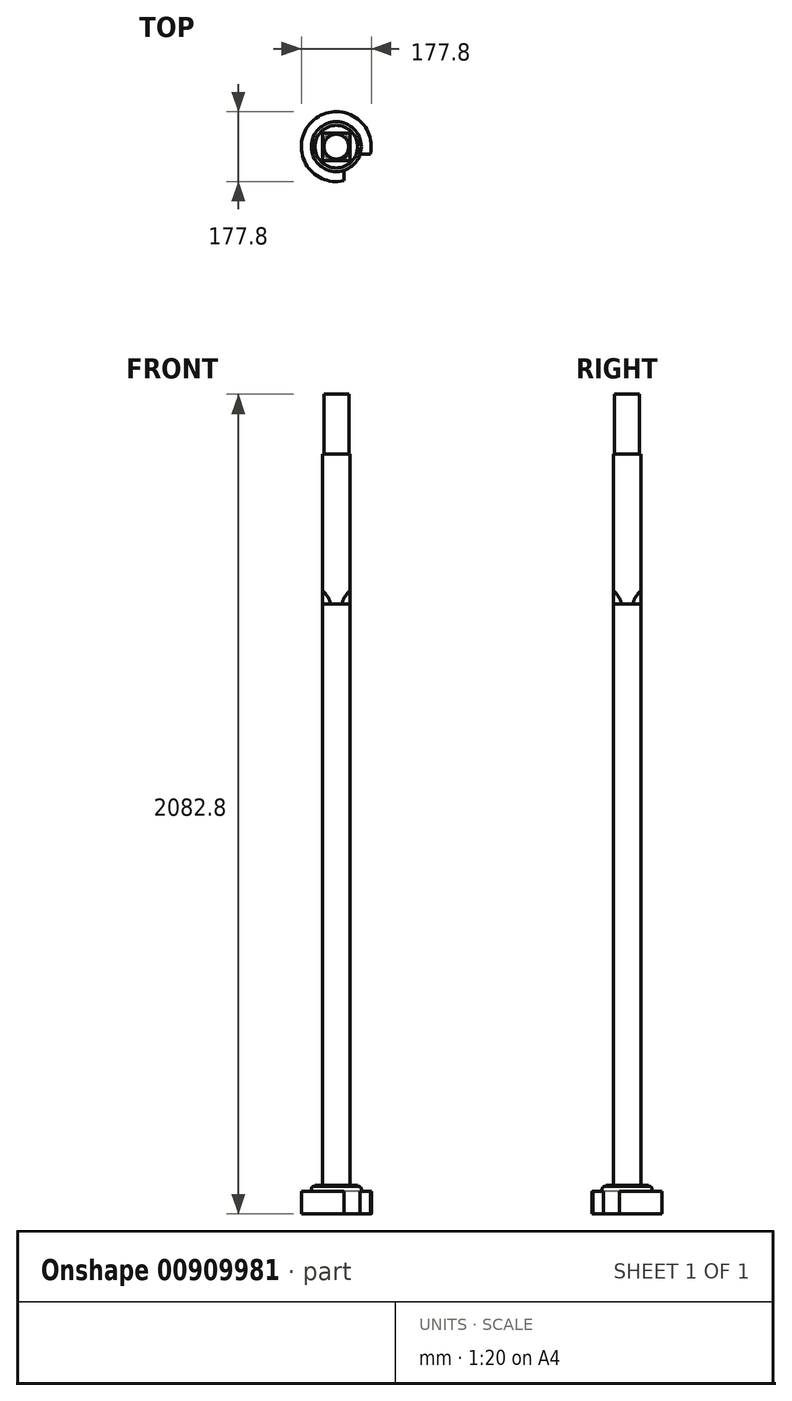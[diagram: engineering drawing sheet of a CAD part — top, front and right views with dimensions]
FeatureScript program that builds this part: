
annotation { "Feature Type Name" : "Feature", "Feature Type Description" : "" }
export const myFeature = defineFeature(function(context is Context, id is Id, definition is map)
    precondition{}
    {
        {
            var Q0;
            Q0=qCreatedBy(makeId("Front.planeOp"),FACE);
            var sketch = newSketch(context, id + "F0", { "sketchPlane" : qUnion([Q0])});
            skLineSegment(sketch, "E0.bottom", {"start": v(0, 0) * mm, "end": v(88.9, 0) * mm});
            skLineSegment(sketch, "E0.top", {"start": v(63.5, 57.15) * mm, "end": v(88.9, 57.15) * mm});
            skLineSegment(sketch, "E0.right", {"start": v(88.9, 0) * mm, "end": v(88.9, 57.15) * mm});
            skLineSegment(sketch, "E1.left", {"start": v(0, 0) * mm, "end": v(0, 1549.4) * mm});
            skLineSegment(sketch, "E1.right", {"start": v(34.92, 0) * mm, "end": v(34.92, 1549.4) * mm});
            skLineSegment(sketch, "E2.bottom", {"start": v(34.92, 1549.4) * mm, "end": v(-34.93, 1549.4) * mm});
            skLineSegment(sketch, "E2.top", {"start": v(34.92, 1930.4) * mm, "end": v(-34.93, 1930.4) * mm});
            skLineSegment(sketch, "E2.left", {"start": v(34.92, 1549.4) * mm, "end": v(34.92, 1930.4) * mm});
            skLineSegment(sketch, "E2.right", {"start": v(-34.93, 1549.4) * mm, "end": v(-34.93, 1930.4) * mm});
            skLineSegment(sketch, "E3", {"start": v(0, 0) * mm, "end": v(0, -15.12) * mm, "construction": true});
            skLineSegment(sketch, "E4.top", {"start": v(0, 2082.8) * mm, "end": v(31.75, 2082.8) * mm});
            skLineSegment(sketch, "E4.left", {"start": v(0, 1930.4) * mm, "end": v(0, 2082.8) * mm});
            skLineSegment(sketch, "E4.right", {"start": v(31.75, 1930.4) * mm, "end": v(31.75, 2082.8) * mm});
            skCircle(sketch, "E5", {"center": v(95.25, 1549.4) * mm, "radius": 57.15 * mm});
            skLineSegment(sketch, "E6", {"start": v(63.5, 57.15) * mm, "end": v(63.5, 63.5) * mm});
            skLineSegment(sketch, "E7", {"start": v(57.15, 69.85) * mm, "end": v(54.07, 69.85) * mm});
            skLineSegment(sketch, "E8", {"start": v(54.07, 69.85) * mm, "end": v(54.07, 73.02) * mm});
            skLineSegment(sketch, "E9", {"start": v(54.07, 73.02) * mm, "end": v(34.92, 73.02) * mm});
            skPoint(sketch, "E10.visualSharp", {"position": v(63.5, 69.85) * mm});
            skArc(sketch, "E10.filletArc", {"start": v(63.5, 63.5) * mm, "mid": v(61.64, 68) * mm, "end": v(57.15, 69.85) * mm});
            skSolve(sketch);
        }
        {
            var Q0;
            Q0=makeQuery(id+"F0.imprint","IMPRINT",FACE,{"disambiguationData":[TD([[makeQuery(id+"F0.imprint","IMPRINT",EDGE,{"derivedFrom":sQuery(id+"F0.wireOp",EDGE,"E0.top")}),-1.0]])]});
            var Q1;
            Q1=sQuery(id+"F0.wireOp",EDGE,"E3");
            revolve(context, id + "F1", {"surfaceOperationType" : NewSurfaceOperationType.NEW, "entities" : qUnion([Q0]), "axis" : qUnion([Q1]), "revolveType" : RevolveType.FULL});
        }
        {
            var Q0;
            {var subQ0=sQuery(id+"F0.wireOp",EDGE,"E1.left");Q0=makeQuery(id+"F0.imprint","IMPRINT",FACE,{"disambiguationData":[TD([[makeQuery(id+"F0.imprint","IMPRINT",EDGE,{"derivedFrom":subQ0}),-1.0]])]});}
            var Q1;
            Q1=sQuery(id+"F0.wireOp",EDGE,"E3");
            revolve(context, id + "F2", {"operationType" : NewBodyOperationType.ADD, "surfaceOperationType" : NewSurfaceOperationType.NEW, "entities" : qUnion([Q0]), "axis" : qUnion([Q1]), "revolveType" : RevolveType.FULL});
        }
        {
            var Q0;
            {var subQ3=sQuery(id+"F0.wireOp",EDGE,"E2.left");Q0=makeQuery(id+"F0.imprint","IMPRINT",FACE,{"disambiguationData":[TD([[makeQuery(id+"F0.imprint","IMPRINT",EDGE,{"derivedFrom":subQ3}),1.0]])]});}
            extrude(context, id + "F3", {"entities" : qUnion([Q0]), "operationType" : NewBodyOperationType.ADD, "flatOperationType" : FlatOperationType.REMOVE, "depth" : 69.85 * mm, "offsetDistance" : 25 * mm, "domain" : OperationDomain.MODEL, "symmetric" : true});
        }
        {
            var Q0;
            Q0=makeQuery(id+"F0.imprint","IMPRINT",FACE,{"disambiguationData":[TD([[makeQuery(id+"F0.imprint","IMPRINT",EDGE,{"derivedFrom":sQuery(id+"F0.wireOp",EDGE,"E4.top")}),-1.0]])]});
            var Q1;
            Q1=sQuery(id+"F0.wireOp",EDGE,"E3");
            revolve(context, id + "F4", {"operationType" : NewBodyOperationType.ADD, "surfaceOperationType" : NewSurfaceOperationType.NEW, "entities" : qUnion([Q0]), "axis" : qUnion([Q1]), "revolveType" : RevolveType.FULL});
        }
        {
            var Q0;
            Q0=makeQuery(id+"F0.imprint","IMPRINT",FACE,{"disambiguationData":[TD([[makeQuery(id+"F0.imprint","IMPRINT",EDGE,{"derivedFrom":sQuery(id+"F0.wireOp",EDGE,"E5")}),1.0]])]});
            var Q1;
            Q1=sQuery(id+"F0.wireOp",EDGE,"E3");
            revolve(context, id + "F5", {"operationType" : NewBodyOperationType.REMOVE, "surfaceOperationType" : NewSurfaceOperationType.NEW, "entities" : qUnion([Q0]), "axis" : qUnion([Q1]), "revolveType" : RevolveType.FULL, "oppositeDirection" : true});
        }
        {
            var Q0;
            {var subQ0=sQuery(id+"F0.wireOp",EDGE,"E0.bottom");Q0=makeQuery(id+"F2.boolean.opBoolean","MERGE",FACE,{"derivedFrom":[makeQuery(id+"F1.opRevolve","SWEPT_FACE",FACE,{"disambiguationData":[OSD([subQ0])]}),makeQuery(id+"F2.opRevolve","SWEPT_FACE",FACE,{"disambiguationData":[OSD([subQ0])]})]});}
            var sketch = newSketch(context, id + "F6", { "sketchPlane" : qUnion([Q0])});
            skArc(sketch, "E11", {"start": v(60.58, 19.05) * mm, "mid": v(44.9, 44.9) * mm, "end": v(19.05, 60.58) * mm});
            skLineSegment(sketch, "E12", {"start": v(60.58, 19.05) * mm, "end": v(86.83, 19.05) * mm});
            skArc(sketch, "E13", {"start": v(86.83, 19.05) * mm, "mid": v(62.86, 62.86) * mm, "end": v(19.05, 86.83) * mm});
            skLineSegment(sketch, "E14", {"start": v(19.05, 86.83) * mm, "end": v(19.05, 60.58) * mm});
            skSolve(sketch);
        }
        {
            var Q0;
            Q0=makeQuery(id+"F6.imprint","IMPRINT",FACE,{"disambiguationData":[TD([[makeQuery(id+"F6.imprint","IMPRINT",EDGE,{"derivedFrom":sQuery(id+"F6.wireOp",EDGE,"E11")}),-1.0]])]});
            var Q1;
            Q1=makeQuery(id+"F1.opRevolve","SWEPT_FACE",FACE,{"disambiguationData":[OSD([sQuery(id+"F0.wireOp",EDGE,"E0.top")])]});
            extrude(context, id + "F7", {"entities" : qUnion([Q0]), "operationType" : NewBodyOperationType.REMOVE, "endBound" : BoundingType.UP_TO_SURFACE, "oppositeDirection" : true, "depth" : 25 * mm, "endBoundEntityFace" : qUnion([Q1]), "offsetDistance" : 25 * mm});
        }
    });
